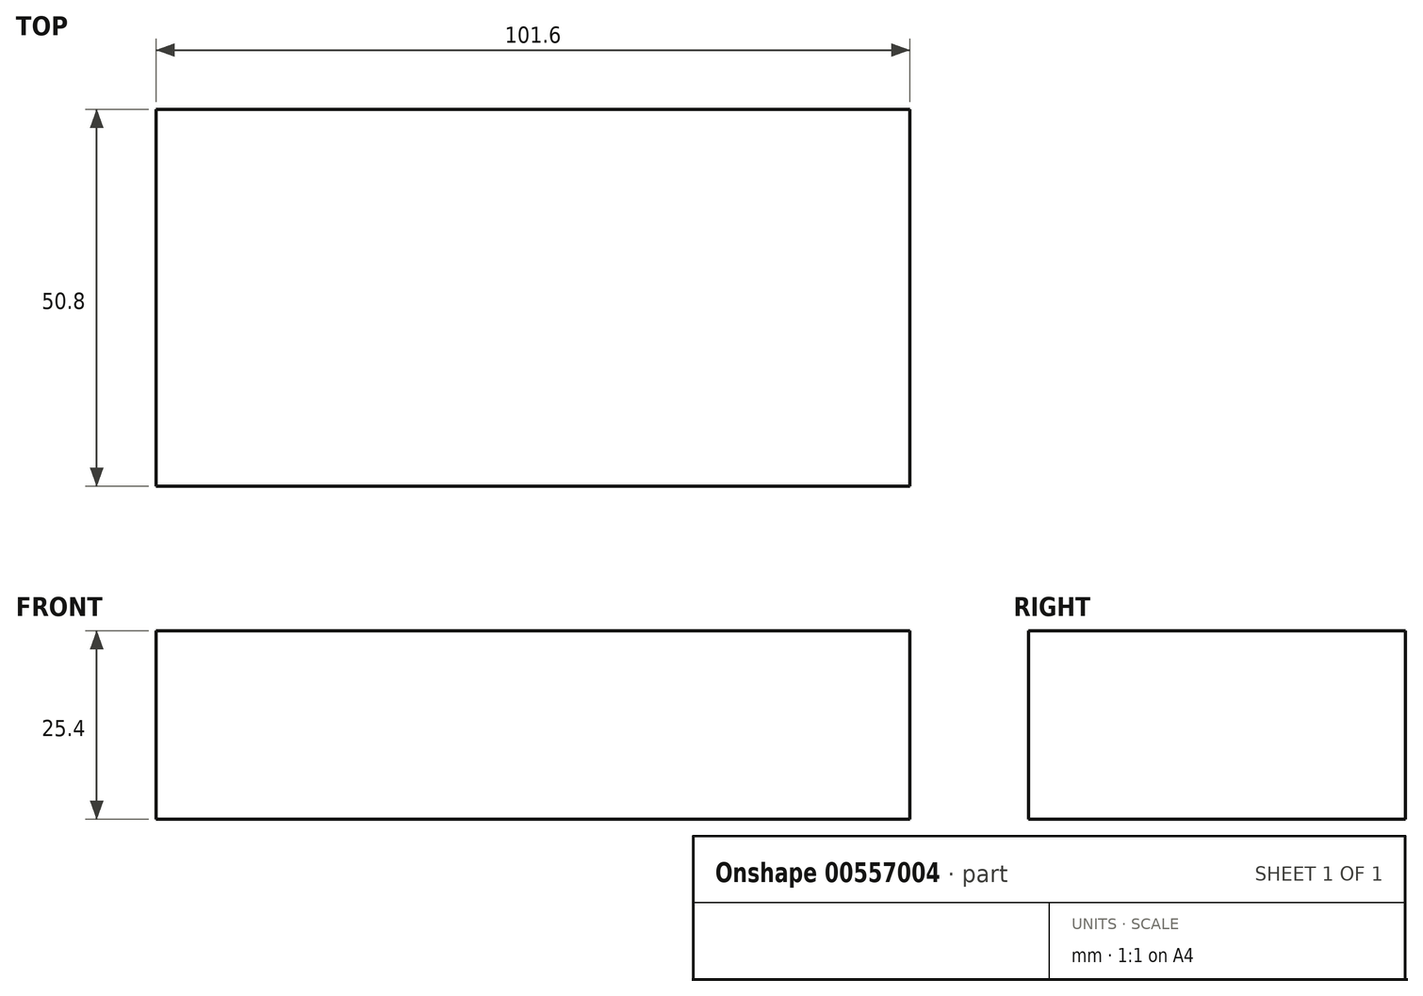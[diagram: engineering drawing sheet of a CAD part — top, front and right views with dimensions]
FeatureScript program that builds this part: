
annotation { "Feature Type Name" : "Feature", "Feature Type Description" : "" }
export const myFeature = defineFeature(function(context is Context, id is Id, definition is map)
    precondition{}
    {
        {
            var Q0;
            Q0=qCreatedBy(makeId("Top.planeOp"),FACE);
            var sketch = newSketch(context, id + "F0", { "sketchPlane" : qUnion([Q0])});
            skLineSegment(sketch, "E0.bottom", {"start": v(-50.8, -25.4) * mm, "end": v(50.8, -25.4) * mm});
            skLineSegment(sketch, "E0.top", {"start": v(-50.8, 25.4) * mm, "end": v(50.8, 25.4) * mm});
            skLineSegment(sketch, "E0.left", {"start": v(-50.8, -25.4) * mm, "end": v(-50.8, 25.4) * mm});
            skLineSegment(sketch, "E0.right", {"start": v(50.8, -25.4) * mm, "end": v(50.8, 25.4) * mm});
            skPoint(sketch, "E0.middle", {"position": v(0, 0) * mm});
            skSolve(sketch);
        }
        {
            var Q0;
            Q0=qSketchRegion(id+"F0",true);
            var Q1;
            Q1=makeQuery(id+"F0.imprint","IMPRINT",FACE,{"disambiguationData":[TD([[makeQuery(id+"F0.imprint","IMPRINT",EDGE,{"derivedFrom":sQuery(id+"F0.wireOp",EDGE,"E0.bottom")}),1.0]])]});
            extrude(context, id + "F1", {"entities" : qUnion([Q0, Q1]), "depth" : 25.4 * mm, "offsetDistance" : 25.4 * mm});
        }
    });
